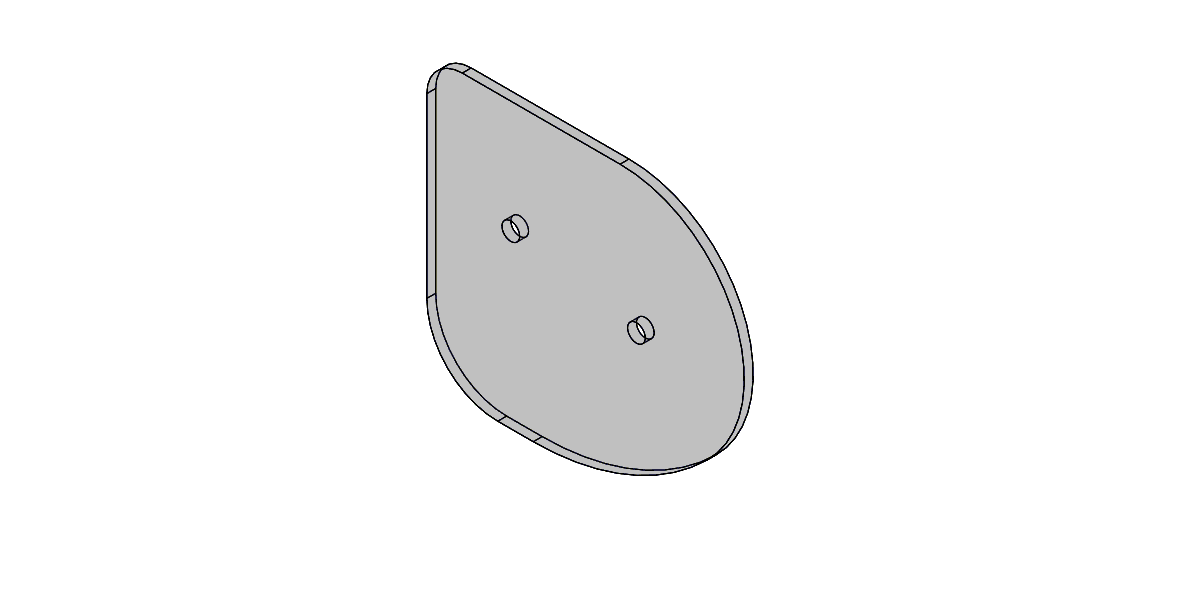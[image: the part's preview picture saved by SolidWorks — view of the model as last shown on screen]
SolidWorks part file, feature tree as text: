
SOLIDWORKS PART (.sldprt)
format: sldprt  version: not decoded by parser v0  size: 151,040 bytes
history: native  units: mm
features: sketch x3, material x1, extrude x1, hole x1 (+13 scaffold rows collapsed)
feature tree (19):
  scaffold x13  (default folders/planes/origin — collapsed)
  material  "Material <not specified>"
  sketch  "Sketch1"  dims[D1=0.0mm]
  extrude  "Boss-Extrude1"  Depth=6.35mm
  hole  "1/2 (0.5) Diameter Hole1"  Diameter=12.7mm Depth=6.35mm
  sketch  "Sketch3"  dims[D1=~89.94775mm D2=~18.110708mm]
  sketch  "Sketch2"  dims[hole-wizard template sketch: 60 standard entries collapsed; hole parameters kept: c18.Thru Hole Depth=6.35mm]
decode coverage: 5 of 5 modeling features carry decoded parameters
note: ~ marks probable driven/reference dimensions
note: suppression state not decoded; provenance and decode notes live in map.json
